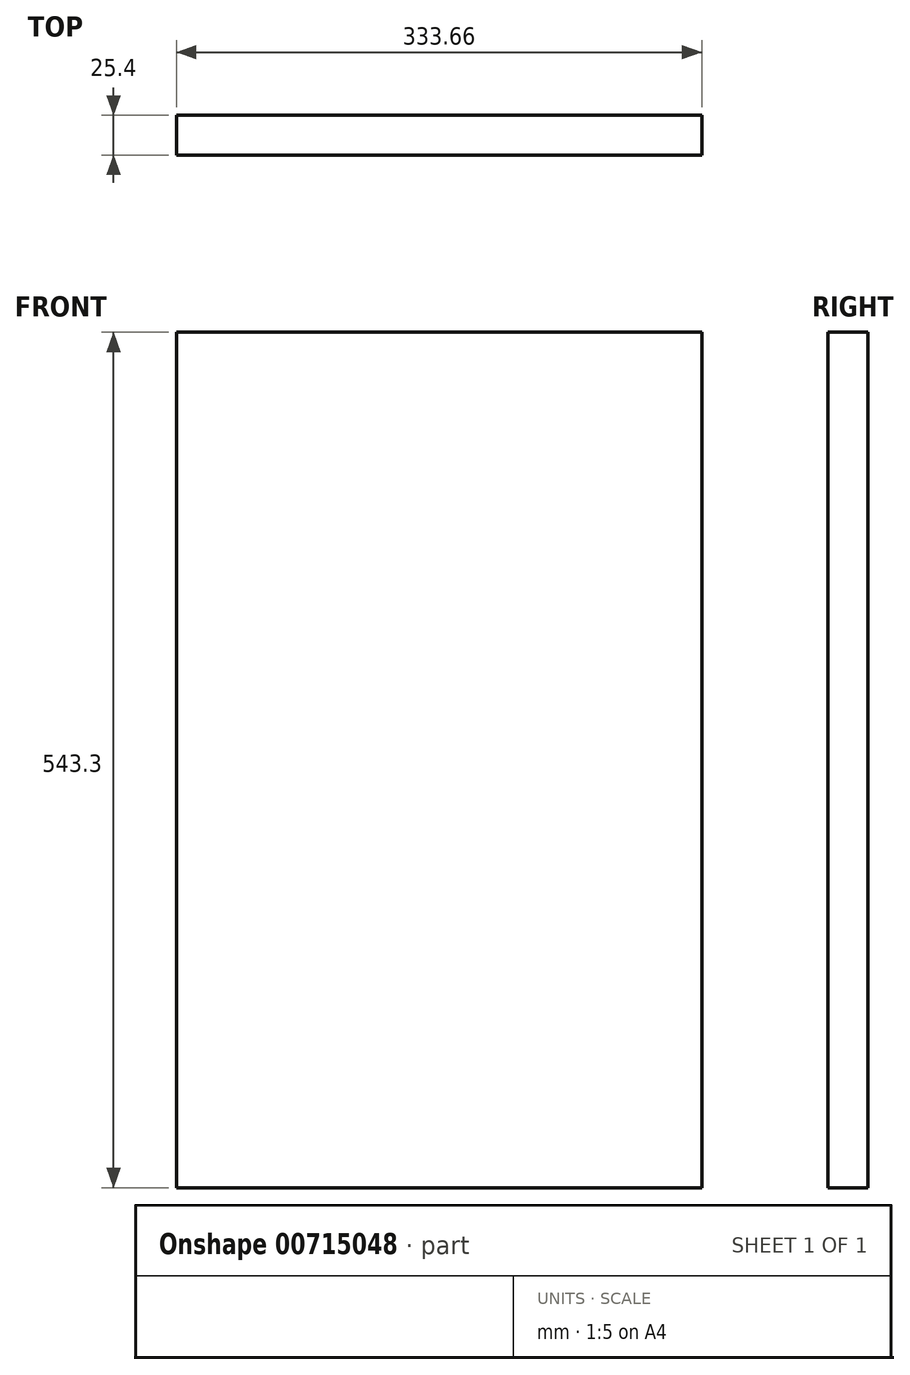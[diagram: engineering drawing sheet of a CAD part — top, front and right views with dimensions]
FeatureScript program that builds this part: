
annotation { "Feature Type Name" : "Feature", "Feature Type Description" : "" }
export const myFeature = defineFeature(function(context is Context, id is Id, definition is map)
    precondition{}
    {
        {
            var Q0;
            Q0=qCreatedBy(makeId("Front.planeOp"),FACE);
            var sketch = newSketch(context, id + "F0", { "sketchPlane" : qUnion([Q0])});
            skLineSegment(sketch, "E0.bottom", {"start": v(-27.13, 30.35) * mm, "end": v(27.13, 30.35) * mm});
            skLineSegment(sketch, "E0.top", {"start": v(-27.13, -30.35) * mm, "end": v(27.13, -30.35) * mm});
            skLineSegment(sketch, "E0.left", {"start": v(-27.13, 30.35) * mm, "end": v(-27.13, -30.35) * mm});
            skLineSegment(sketch, "E0.right", {"start": v(27.13, 30.35) * mm, "end": v(27.13, -30.35) * mm});
            skPoint(sketch, "E0.middle", {"position": v(0, 0) * mm});
            skSolve(sketch);
        }
        {
            var Q0;
            Q0=makeQuery(id+"F0.imprint","IMPRINT",FACE,{"disambiguationData":[TD([[makeQuery(id+"F0.imprint","IMPRINT",EDGE,{"derivedFrom":sQuery(id+"F0.wireOp",EDGE,"E0.bottom")}),-1.0]])]});
            extrude(context, id + "F1", {"entities" : qUnion([Q0]), "depth" : 25.4 * mm, "offsetDistance" : 25.4 * mm});
        }
        {
            var Q0;
            Q0=makeQuery(id+"F1.opExtrude","SWEPT_FACE",FACE,{"disambiguationData":[OSD([sQuery(id+"F0.wireOp",EDGE,"E0.bottom")])]});
            extrude(context, id + "F2", {"entities" : qUnion([Q0]), "operationType" : NewBodyOperationType.ADD, "depth" : 482.6 * mm, "offsetDistance" : 25.4 * mm});
        }
        {
            var Q0;
            {var subQ0=sQuery(id+"F0.wireOp",EDGE,"E0.right");Q0=makeQuery(id+"F2.boolean.opBoolean","MERGE",FACE,{"derivedFrom":[makeQuery(id+"F1.opExtrude","SWEPT_FACE",FACE,{"disambiguationData":[OSD([subQ0])]}),makeQuery(id+"F2.opExtrude","SWEPT_FACE",FACE,{"disambiguationData":[OSD([sQuery(id+"F0.wireOp",EDGE,"E0.bottom"),subQ0])]})]});}
            extrude(context, id + "F3", {"entities" : qUnion([Q0]), "operationType" : NewBodyOperationType.ADD, "depth" : 279.4 * mm, "offsetDistance" : 25.4 * mm});
        }
    });
